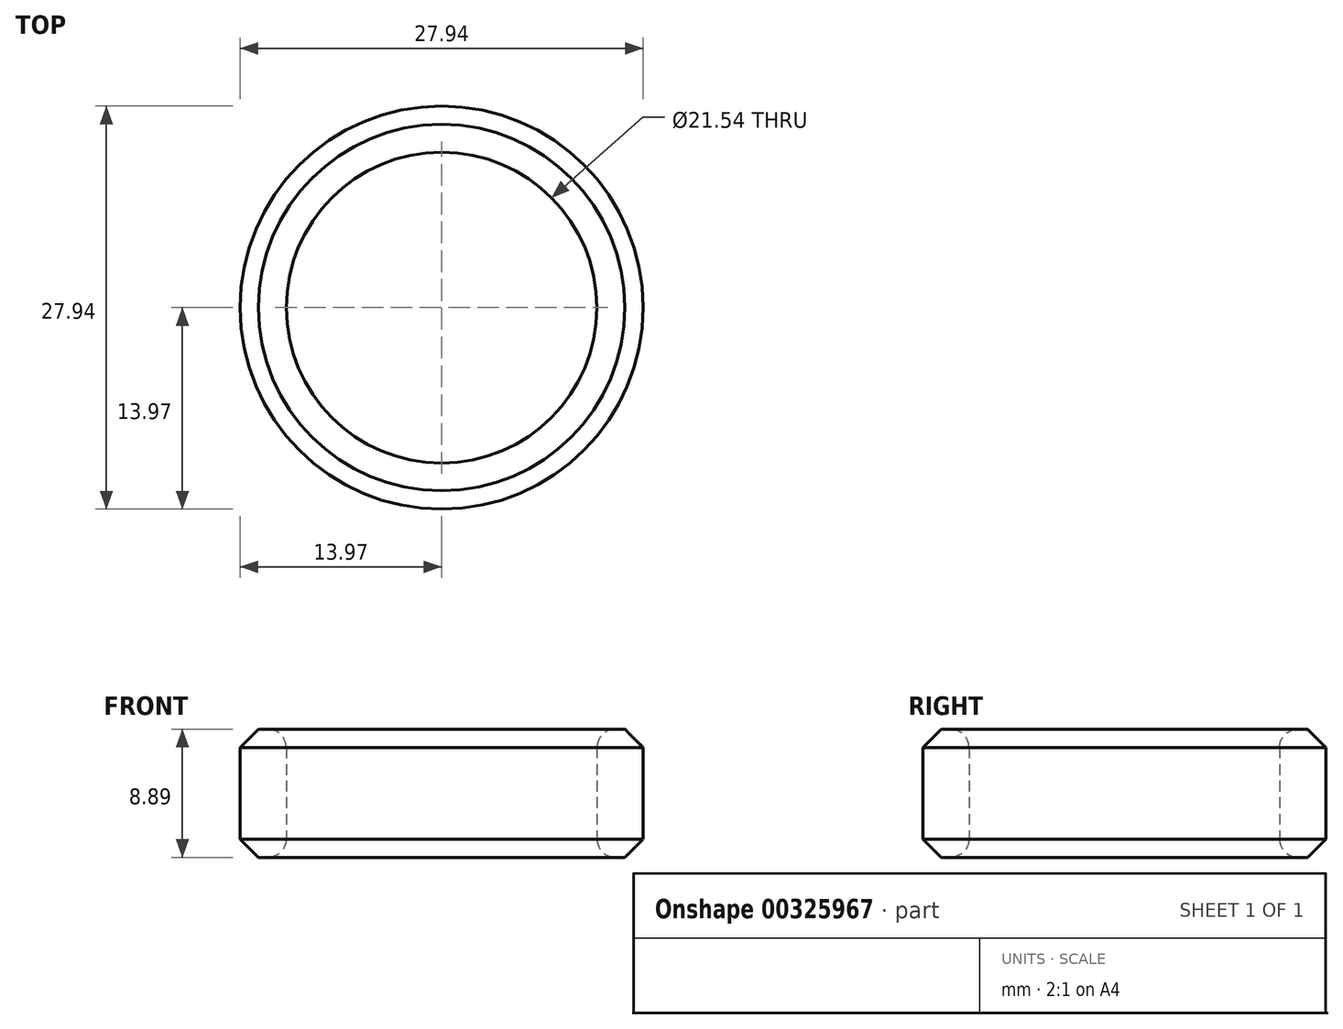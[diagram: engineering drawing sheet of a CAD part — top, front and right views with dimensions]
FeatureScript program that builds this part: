
annotation { "Feature Type Name" : "Feature", "Feature Type Description" : "" }
export const myFeature = defineFeature(function(context is Context, id is Id, definition is map)
    precondition{}
    {
        {
            var Q0;
            Q0=qCreatedBy(makeId("Top.planeOp"),FACE);
            var sketch = newSketch(context, id + "F0", { "sketchPlane" : qUnion([Q0])});
            skCircle(sketch, "E0.0", {"center": v(0, 0) * mm, "radius": 13.97 * mm});
            skCircle(sketch, "E1.0", {"center": v(0, 0) * mm, "radius": 10.77 * mm});
            skSolve(sketch);
        }
        {
            var Q0;
            Q0=makeQuery(id+"F0.imprint","IMPRINT",FACE,{"disambiguationData":[TD([[makeQuery(id+"F0.imprint","IMPRINT",EDGE,{"derivedFrom":sQuery(id+"F0.wireOp",EDGE,"E0.0")}),1.0]])]});
            extrude(context, id + "F1", {"entities" : qUnion([Q0]), "depth" : 8.9 * mm});
        }
        {
            var Q0;
            Q0=makeQuery(id+"F1.opExtrude","CAP_EDGE",EDGE,{"disambiguationData":[OSD([sQuery(id+"F0.wireOp",EDGE,"E1.0")])],"isStart":false});
            var Q1;
            Q1=makeQuery(id+"F1.opExtrude","CAP_EDGE",EDGE,{"disambiguationData":[OSD([sQuery(id+"F0.wireOp",EDGE,"E1.0")])],"isStart":true});
            fillet(context, id + "F2", {"entities" : qUnion([Q0, Q1]), "radius" : 1.27 * mm, "tangentPropagation" : true, "allowEdgeOverflow" : false});
        }
        {
            var Q0;
            Q0=makeQuery(id+"F1.opExtrude","SWEPT_FACE",FACE,{"disambiguationData":[OSD([sQuery(id+"F0.wireOp",EDGE,"E0.0")])]});
            chamfer(context, id + "F3", {"entities" : qUnion([Q0]), "width" : 1.27 * mm, "tangentPropagation" : true});
        }
    });
